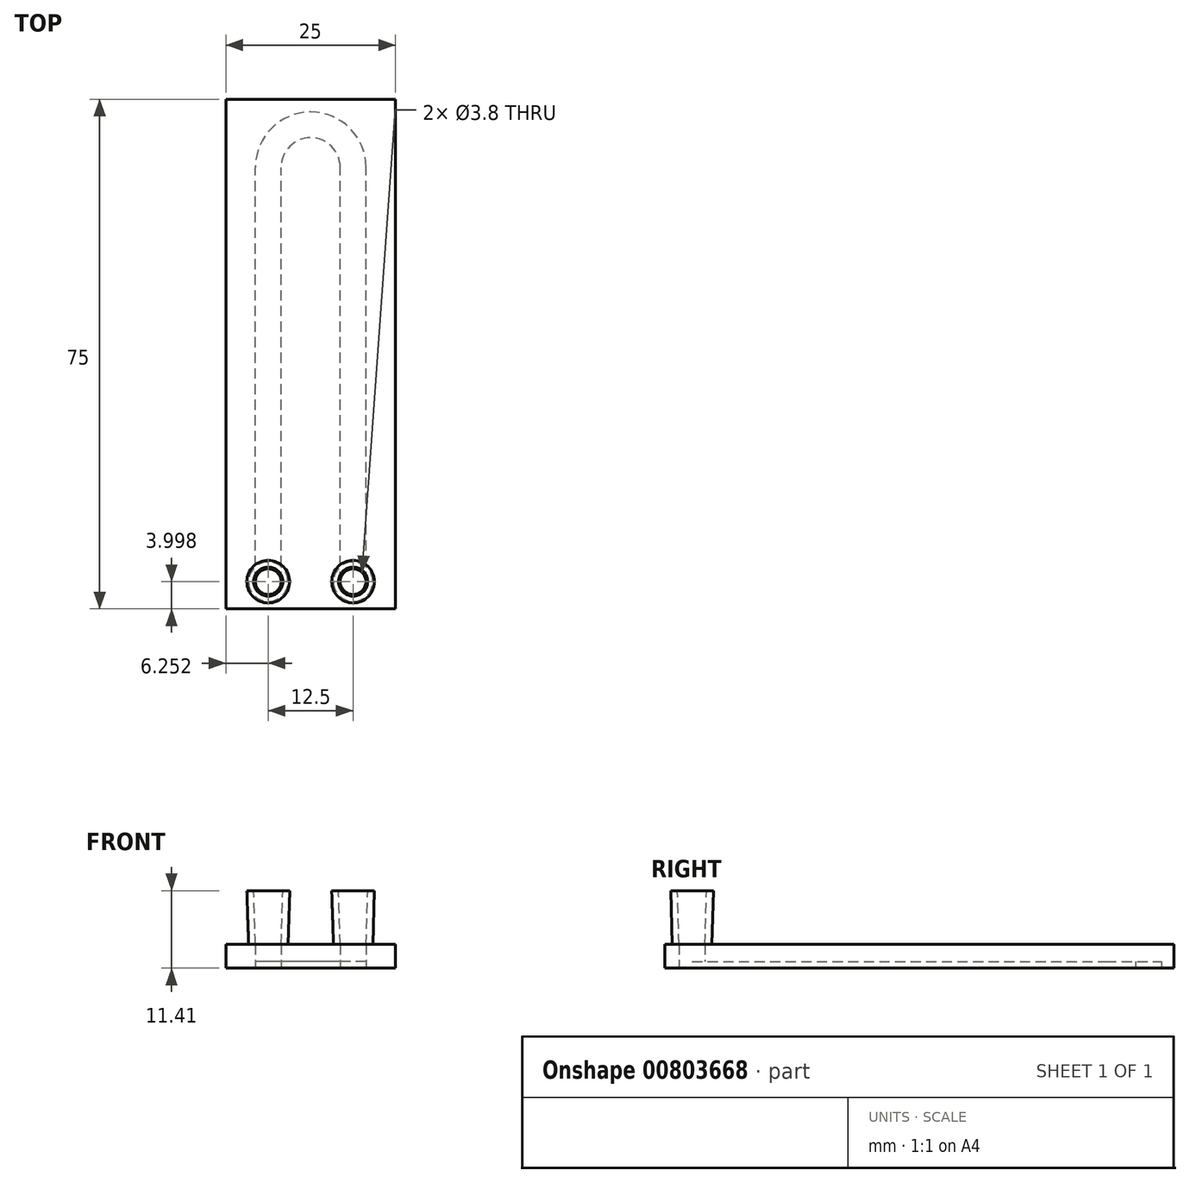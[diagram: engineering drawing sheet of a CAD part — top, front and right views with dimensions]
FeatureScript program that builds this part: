
annotation { "Feature Type Name" : "Feature", "Feature Type Description" : "" }
export const myFeature = defineFeature(function(context is Context, id is Id, definition is map)
    precondition{}
    {
        {
            var Q0;
            Q0=qCreatedBy(makeId("Top.planeOp"),FACE);
            var sketch = newSketch(context, id + "F0", { "sketchPlane" : qUnion([Q0])});
            skLineSegment(sketch, "E0.bottom", {"start": v(-44.29, 25.1) * mm, "end": v(-19.29, 25.1) * mm});
            skLineSegment(sketch, "E0.top", {"start": v(-44.29, -49.9) * mm, "end": v(-19.29, -49.9) * mm});
            skLineSegment(sketch, "E0.left", {"start": v(-44.29, 25.1) * mm, "end": v(-44.29, -49.9) * mm});
            skLineSegment(sketch, "E0.right", {"start": v(-19.29, 25.1) * mm, "end": v(-19.29, -49.9) * mm});
            skPoint(sketch, "E1", {"position": v(-31.79, -49.9) * mm});
            skPoint(sketch, "E2", {"position": v(-19.29, -12.4) * mm});
            skPoint(sketch, "E3", {"position": v(-44.29, -12.4) * mm});
            skPoint(sketch, "E4", {"position": v(-31.79, 25.1) * mm});
            skPoint(sketch, "E5", {"position": v(-31.79, -12.4) * mm});
            skPoint(sketch, "E6", {"position": v(-25.54, -49.9) * mm});
            skPoint(sketch, "E7", {"position": v(-38.04, -49.9) * mm});
            skPoint(sketch, "E8", {"position": v(-25.54, -43.64) * mm});
            skPoint(sketch, "E9", {"position": v(-38.04, -43.64) * mm});
            skSolve(sketch);
        }
        {
            var Q0;
            Q0=makeQuery(id+"F0.imprint","IMPRINT",FACE,{"disambiguationData":[TD([[makeQuery(id+"F0.imprint","IMPRINT",EDGE,{"derivedFrom":sQuery(id+"F0.wireOp",EDGE,"E0.bottom")}),-1.0]])]});
            var sketch = newSketch(context, id + "F1", { "sketchPlane" : qUnion([Q0])});
            skPoint(sketch, "E10", {"position": v(-25.54, -45.9) * mm});
            skPoint(sketch, "E11", {"position": v(-38.04, -45.9) * mm});
            skPoint(sketch, "E12", {"position": v(-31.79, 23.1) * mm});
            skPoint(sketch, "E13", {"position": v(-31.79, 15.1) * mm});
            skCircle(sketch, "E14", {"center": v(-25.54, -45.9) * mm, "radius": 1.9 * mm});
            skCircle(sketch, "E15", {"center": v(-38.04, -45.9) * mm, "radius": 1.9 * mm});
            skPoint(sketch, "E16", {"position": v(-23.64, -45.9) * mm});
            skPoint(sketch, "E17", {"position": v(-27.44, -45.9) * mm});
            skPoint(sketch, "E18", {"position": v(-36.14, -45.9) * mm});
            skPoint(sketch, "E19", {"position": v(-39.94, -45.9) * mm});
            skPoint(sketch, "E20", {"position": v(-27.44, 15.1) * mm});
            skPoint(sketch, "E21", {"position": v(-23.64, 15.1) * mm});
            skPoint(sketch, "E22", {"position": v(-39.94, 15.1) * mm});
            skPoint(sketch, "E23", {"position": v(-36.14, 15.1) * mm});
            skArc(sketch, "E24", {"start": v(-23.64, 15.1) * mm, "mid": v(-31.79, 23.26) * mm, "end": v(-39.94, 15.1) * mm});
            skArc(sketch, "E25", {"start": v(-27.44, 15.1) * mm, "mid": v(-31.79, 19.46) * mm, "end": v(-36.14, 15.1) * mm});
            skLineSegment(sketch, "E26", {"start": v(-23.64, -45.9) * mm, "end": v(-23.64, 15.1) * mm});
            skLineSegment(sketch, "E27", {"start": v(-27.44, -45.9) * mm, "end": v(-27.44, 15.1) * mm});
            skLineSegment(sketch, "E28", {"start": v(-36.14, -45.9) * mm, "end": v(-36.14, 15.1) * mm});
            skLineSegment(sketch, "E29", {"start": v(-39.94, -45.9) * mm, "end": v(-39.94, 15.1) * mm});
            skSolve(sketch);
        }
        {
            var Q0;
            Q0=qCreatedBy(makeId("Top.planeOp"),FACE);
            var sketch = newSketch(context, id + "F2", { "sketchPlane" : qUnion([Q0])});
            skPoint(sketch, "E30", {"position": v(-38.04, -45.9) * mm});
            skPoint(sketch, "E31", {"position": v(-25.54, -45.9) * mm});
            skCircle(sketch, "E32", {"center": v(-38.04, -45.9) * mm, "radius": 1.9 * mm});
            skCircle(sketch, "E33", {"center": v(-38.04, -45.9) * mm, "radius": 2.13 * mm});
            skCircle(sketch, "E34", {"center": v(-25.54, -45.9) * mm, "radius": 1.9 * mm});
            skCircle(sketch, "E35", {"center": v(-25.54, -45.9) * mm, "radius": 2.13 * mm});
            skSolve(sketch);
        }
        {
            var Q0;
            Q0 = qSketchRegion(id + "F0", true);
            extrude(context, id + "F3", {"entities" : qUnion([Q0]), "depth" : 3.5 * mm, "offsetDistance" : 25 * mm});
        }
        {
            var Q0;
            Q0 = qSketchRegion(id + "F1", true);
            extrude(context, id + "F4", {"entities" : qUnion([Q0]), "operationType" : NewBodyOperationType.REMOVE, "depth" : 1 * mm, "offsetDistance" : 25 * mm});
        }
        {
            var Q0;
            Q0=makeQuery(id+"F2.imprint","IMPRINT",FACE,{"disambiguationData":[TD([[makeQuery(id+"F2.imprint","IMPRINT",EDGE,{"derivedFrom":sQuery(id+"F2.wireOp",EDGE,"E34")}),1.0]])]});
            var Q1;
            {var subQ0=sQuery(id+"F1.wireOp",EDGE,"E15");var subQ1=makeQuery(id+"F1.imprint","INTERSECT",VERTEX,{"derivedFrom":[subQ0,sQuery(id+"F1.wireOp",EDGE,"E28")]});Q1=makeQuery(id+"F1.imprint","IMPRINT",FACE,{"disambiguationData":[TD([[makeQuery(id+"F1.imprint","IMPRINT",EDGE,{"disambiguationData":[TD([[subQ1,-1.0]])],"derivedFrom":subQ0}),1.0]])]});}
            extrude(context, id + "F5", {"entities" : qUnion([Q0, Q1]), "operationType" : NewBodyOperationType.REMOVE, "depth" : 3.5 * mm, "offsetDistance" : 25 * mm});
        }
        {
            var Q0;
            Q0=qCreatedBy(makeId("Front.planeOp"),FACE);
            cPlane(context, id + "F6", {"entities" : qUnion([Q0]), "cplaneType" : CPlaneType.OFFSET, "offset" : 45.9 * mm, "width" : 150 * mm, "height" : 150 * mm});
        }
        {
            var Q0;
            Q0=qCreatedBy(id+"F6.planeOp",FACE);
            var sketch = newSketch(context, id + "F7", { "sketchPlane" : qUnion([Q0])});
            skPoint(sketch, "E36", {"position": v(-38.04, 3.5) * mm});
            skPoint(sketch, "E37", {"position": v(-25.53, 3.53) * mm});
            skLineSegment(sketch, "E38", {"start": v(-38.04, 3.5) * mm, "end": v(-38.04, 11.4) * mm, "construction": true});
            skLineSegment(sketch, "E39", {"start": v(-38.04, 3.5) * mm, "end": v(-35.14, 3.5) * mm, "construction": true});
            skPoint(sketch, "E40", {"position": v(-35.14, 3.5) * mm});
            skPoint(sketch, "E41", {"position": v(-36.14, 3.5) * mm});
            skPoint(sketch, "E42", {"position": v(-35.9, 11.4) * mm});
            skPoint(sketch, "E43", {"position": v(-34.9, 11.4) * mm});
            skLineSegment(sketch, "E44", {"start": v(-36.14, 3.5) * mm, "end": v(-35.14, 3.5) * mm});
            skLineSegment(sketch, "E45", {"start": v(-34.9, 11.4) * mm, "end": v(-35.9, 11.4) * mm});
            skLineSegment(sketch, "E46", {"start": v(-35.9, 11.4) * mm, "end": v(-36.14, 3.5) * mm});
            skLineSegment(sketch, "E47", {"start": v(-35.14, 3.5) * mm, "end": v(-34.9, 11.4) * mm});
            skSolve(sketch);
        }
        {
            var Q0;
            Q0=makeQuery(id+"F7.imprint","IMPRINT",FACE,{"disambiguationData":[TD([[makeQuery(id+"F7.imprint","IMPRINT",EDGE,{"derivedFrom":sQuery(id+"F7.wireOp",EDGE,"E45")}),1.0]])]});
            var Q1;
            Q1=sQuery(id+"F7.wireOp",EDGE,"E38");
            revolve(context, id + "F8", {"surfaceOperationType" : NewSurfaceOperationType.NEW, "entities" : qUnion([Q0]), "axis" : qUnion([Q1]), "revolveType" : RevolveType.FULL});
        }
        {
            var Q0;
            Q0=qCreatedBy(id+"F6.planeOp",FACE);
            var sketch = newSketch(context, id + "F9", { "sketchPlane" : qUnion([Q0])});
            skPoint(sketch, "E48", {"position": v(-25.54, 3.5) * mm});
            skLineSegment(sketch, "E49", {"start": v(-25.54, 3.5) * mm, "end": v(-25.54, 13.34) * mm, "construction": true});
            skLineSegment(sketch, "E50", {"start": v(-25.54, 3.5) * mm, "end": v(-20.15, 3.5) * mm, "construction": true});
            skPoint(sketch, "E51", {"position": v(-23.64, 3.5) * mm});
            skPoint(sketch, "E52", {"position": v(-22.64, 3.5) * mm});
            skPoint(sketch, "E53", {"position": v(-25.54, 11.4) * mm});
            skPoint(sketch, "E54", {"position": v(-23.4, 11.4) * mm});
            skPoint(sketch, "E55", {"position": v(-22.4, 11.4) * mm});
            skLineSegment(sketch, "E56", {"start": v(-23.64, 3.5) * mm, "end": v(-22.64, 3.5) * mm});
            skLineSegment(sketch, "E57", {"start": v(-22.4, 11.4) * mm, "end": v(-23.4, 11.4) * mm});
            skLineSegment(sketch, "E58", {"start": v(-23.4, 11.4) * mm, "end": v(-23.64, 3.5) * mm});
            skLineSegment(sketch, "E59", {"start": v(-22.64, 3.5) * mm, "end": v(-22.4, 11.4) * mm});
            skSolve(sketch);
        }
        {
            var Q0;
            Q0=makeQuery(id+"F9.imprint","IMPRINT",FACE,{"disambiguationData":[TD([[makeQuery(id+"F9.imprint","IMPRINT",EDGE,{"derivedFrom":sQuery(id+"F9.wireOp",EDGE,"E57")}),1.0]])]});
            var Q1;
            Q1=sQuery(id+"F9.wireOp",EDGE,"E49");
            revolve(context, id + "F10", {"surfaceOperationType" : NewSurfaceOperationType.NEW, "entities" : qUnion([Q0]), "axis" : qUnion([Q1]), "revolveType" : RevolveType.FULL});
        }
    });
